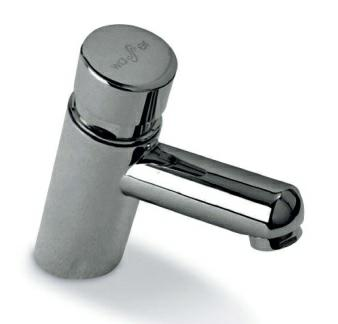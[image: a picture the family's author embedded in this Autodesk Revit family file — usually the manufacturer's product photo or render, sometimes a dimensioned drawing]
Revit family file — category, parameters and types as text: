
# Revit family: CW8002001
name_source: partatom
category: Plumbing Fixtures
revit_build: Autodesk Revit 2016 (Build: 20150220_1215(x64)
units: mm (PartAtom-declared; Revit-internal decimal feet)

## family parameters
Always vertical = Yes
Cut with Voids When Loaded = No
OmniClass Number = 23.45.00.00
OmniClass Title = Sanitary, Laundry, and Cleaning Equipment
Part Type = Normal
Room Calculation Point = No
Round Connector Dimension = Use Diameter
Shared = No
Work Plane-Based = No

## types (1)
- 135 x 119
    Assembly Code = D2010
    CW Connection = Yes
    Description = Grifo temporizado inclinado para lavabo 1/2"
    HW Connection = No
    Height = 800 mm  [stored 2.62467 ft]
    Manufacturer = CHC
    Material = Stainless Steel, Polished
    Model = CW8002001
    Type Image = CW8002001.jpg
    URL = www.grupochc.cl
    Vent Connection = No
    Waste Connection = No

note: [stored X ft] marks values corroborated as IEEE doubles in the binary element streams (Revit-internal decimal feet)

## geometry (parser evidence)
native form markers: Sweep x2
no freeform markers — native parametric forms only
